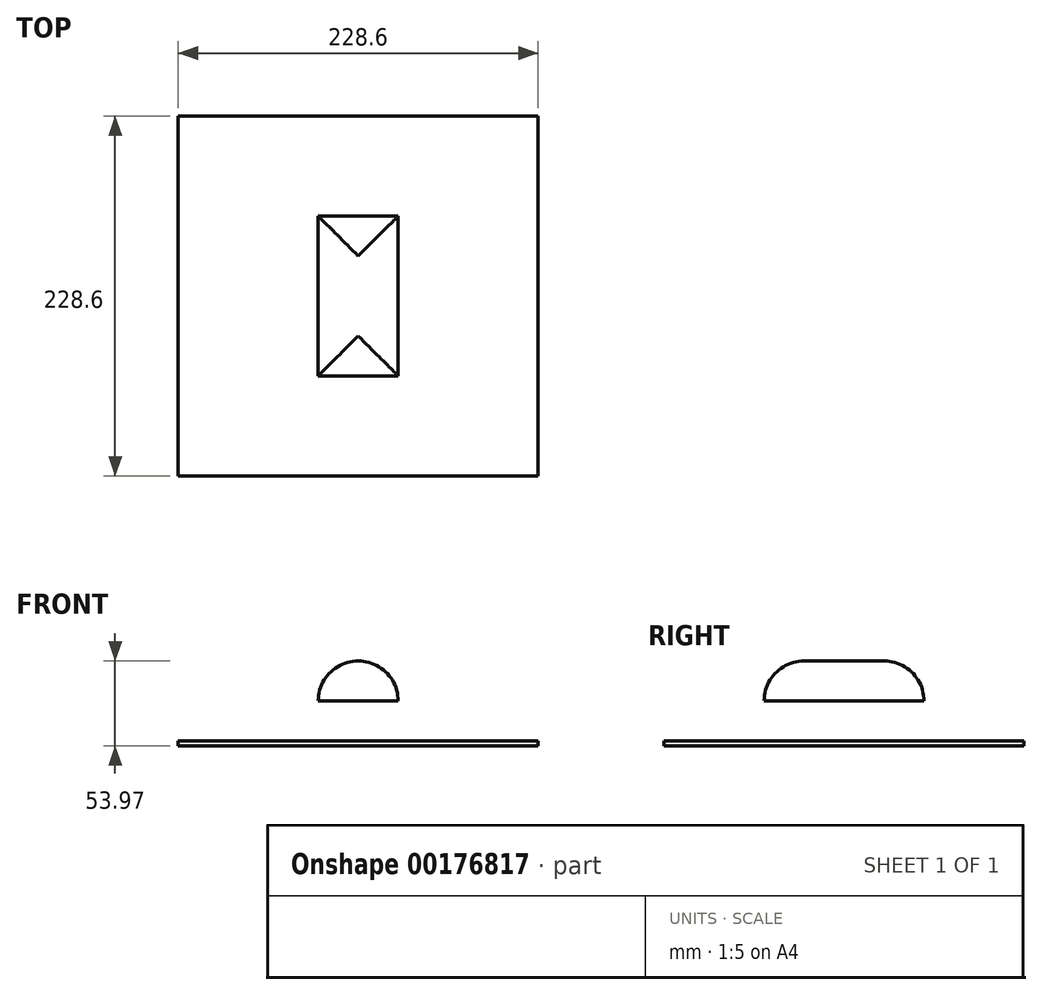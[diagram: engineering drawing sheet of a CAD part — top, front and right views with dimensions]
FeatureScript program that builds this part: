
annotation { "Feature Type Name" : "Feature", "Feature Type Description" : "" }
export const myFeature = defineFeature(function(context is Context, id is Id, definition is map)
    precondition{}
    {
        {
            var Q0;
            Q0=qCreatedBy(makeId("Top.planeOp"),FACE);
            var sketch = newSketch(context, id + "F0", { "sketchPlane" : qUnion([Q0])});
            skLineSegment(sketch, "E0.bottom", {"start": v(25.4, 50.8) * mm, "end": v(-25.4, 50.8) * mm});
            skLineSegment(sketch, "E0.top", {"start": v(25.4, -50.8) * mm, "end": v(-25.4, -50.8) * mm});
            skLineSegment(sketch, "E0.left", {"start": v(25.4, 50.8) * mm, "end": v(25.4, -50.8) * mm});
            skLineSegment(sketch, "E0.right", {"start": v(-25.4, 50.8) * mm, "end": v(-25.4, -50.8) * mm});
            skPoint(sketch, "E0.middle", {"position": v(0, 0) * mm});
            skSolve(sketch);
        }
        {
            var Q0;
            Q0 = qSketchRegion(id + "F0", true);
            extrude(context, id + "F1", {"entities" : qUnion([Q0]), "depth" : 25.4 * mm});
        }
        {
            var Q0;
            Q0=makeQuery(id+"F1.opExtrude","CAP_EDGE",EDGE,{"disambiguationData":[OSD([sQuery(id+"F0.wireOp",EDGE,"E0.right")])],"isStart":false});
            var Q1;
            Q1=makeQuery(id+"F1.opExtrude","CAP_EDGE",EDGE,{"disambiguationData":[OSD([sQuery(id+"F0.wireOp",EDGE,"E0.top")])],"isStart":false});
            var Q2;
            Q2=makeQuery(id+"F1.opExtrude","CAP_EDGE",EDGE,{"disambiguationData":[OSD([sQuery(id+"F0.wireOp",EDGE,"E0.left")])],"isStart":false});
            var Q3;
            Q3=makeQuery(id+"F1.opExtrude","CAP_EDGE",EDGE,{"disambiguationData":[OSD([sQuery(id+"F0.wireOp",EDGE,"E0.bottom")])],"isStart":false});
            fillet(context, id + "F2", {"entities" : qUnion([Q0, Q1, Q2, Q3]), "radius" : 25.4 * mm, "tangentPropagation" : true, "allowEdgeOverflow" : false});
        }
        {
            var Q0;
            Q0=qCreatedBy(makeId("Top.planeOp"),FACE);
            cPlane(context, id + "F3", {"entities" : qUnion([Q0]), "cplaneType" : CPlaneType.OFFSET, "offset" : 25.4 * mm, "oppositeDirection" : true, "width" : 152.4 * mm, "height" : 152.4 * mm});
        }
        {
            var Q0;
            Q0=qCreatedBy(id+"F3.planeOp",FACE);
            var sketch = newSketch(context, id + "F4", { "sketchPlane" : qUnion([Q0])});
            skLineSegment(sketch, "E1.bottom", {"start": v(114.3, 114.3) * mm, "end": v(-114.3, 114.3) * mm});
            skLineSegment(sketch, "E1.top", {"start": v(114.3, -114.3) * mm, "end": v(-114.3, -114.3) * mm});
            skLineSegment(sketch, "E1.left", {"start": v(114.3, 114.3) * mm, "end": v(114.3, -114.3) * mm});
            skLineSegment(sketch, "E1.right", {"start": v(-114.3, 114.3) * mm, "end": v(-114.3, -114.3) * mm});
            skPoint(sketch, "E1.middle", {"position": v(0, 0) * mm});
            skSolve(sketch);
        }
        {
            var Q0;
            Q0 = qSketchRegion(id + "F4", true);
            extrude(context, id + "F5", {"entities" : qUnion([Q0]), "oppositeDirection" : true, "depth" : 3.17 * mm});
        }
    });
